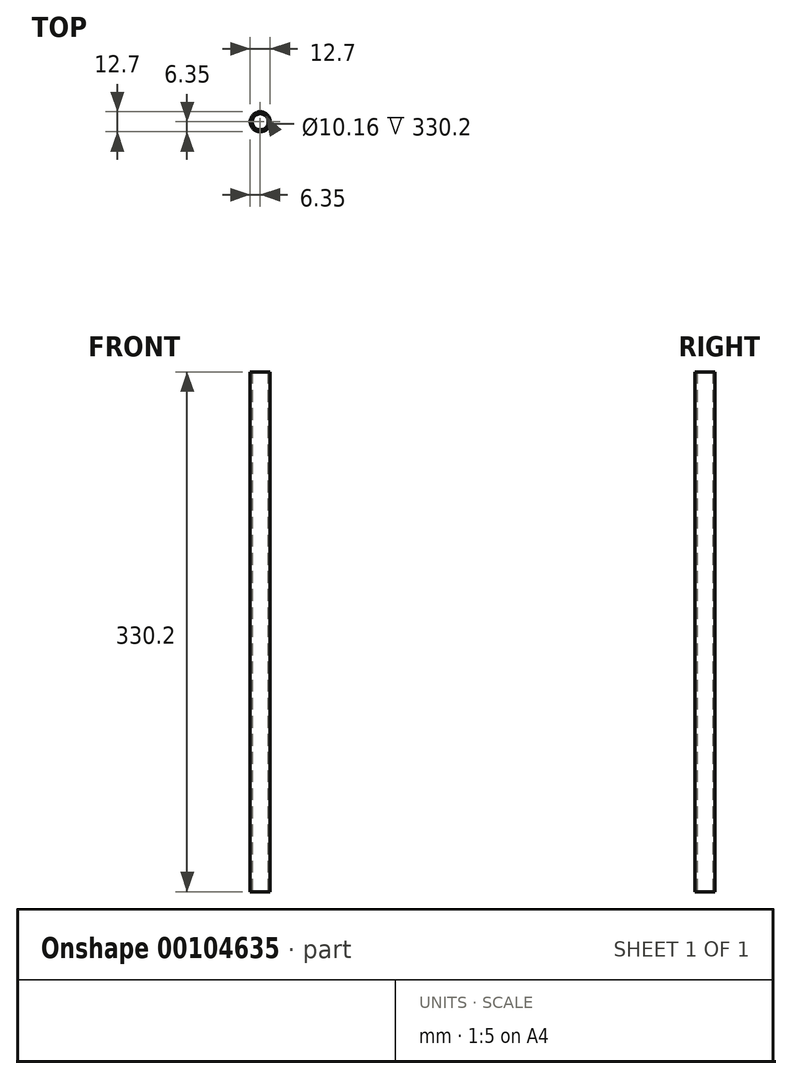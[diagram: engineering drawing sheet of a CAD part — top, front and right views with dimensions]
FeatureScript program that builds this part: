
annotation { "Feature Type Name" : "Feature", "Feature Type Description" : "" }
export const myFeature = defineFeature(function(context is Context, id is Id, definition is map)
    precondition{}
    {
        {
            var Q0;
            Q0=qCreatedBy(makeId("Top.planeOp"),FACE);
            var sketch = newSketch(context, id + "F0", { "sketchPlane" : qUnion([Q0])});
            skCircle(sketch, "E0", {"center": v(0, 0) * mm, "radius": 6.35 * mm});
            skCircle(sketch, "E1", {"center": v(0, 0) * mm, "radius": 5.08 * mm});
            skSolve(sketch);
        }
        {
            var Q0;
            Q0=makeQuery(id+"F0.imprint","IMPRINT",FACE,{"disambiguationData":[TD([[makeQuery(id+"F0.imprint","IMPRINT",EDGE,{"derivedFrom":sQuery(id+"F0.wireOp",EDGE,"E0")}),1.0]])]});
            extrude(context, id + "F1", {"entities" : qUnion([Q0]), "depth" : 330.2 * mm});
        }
    });
